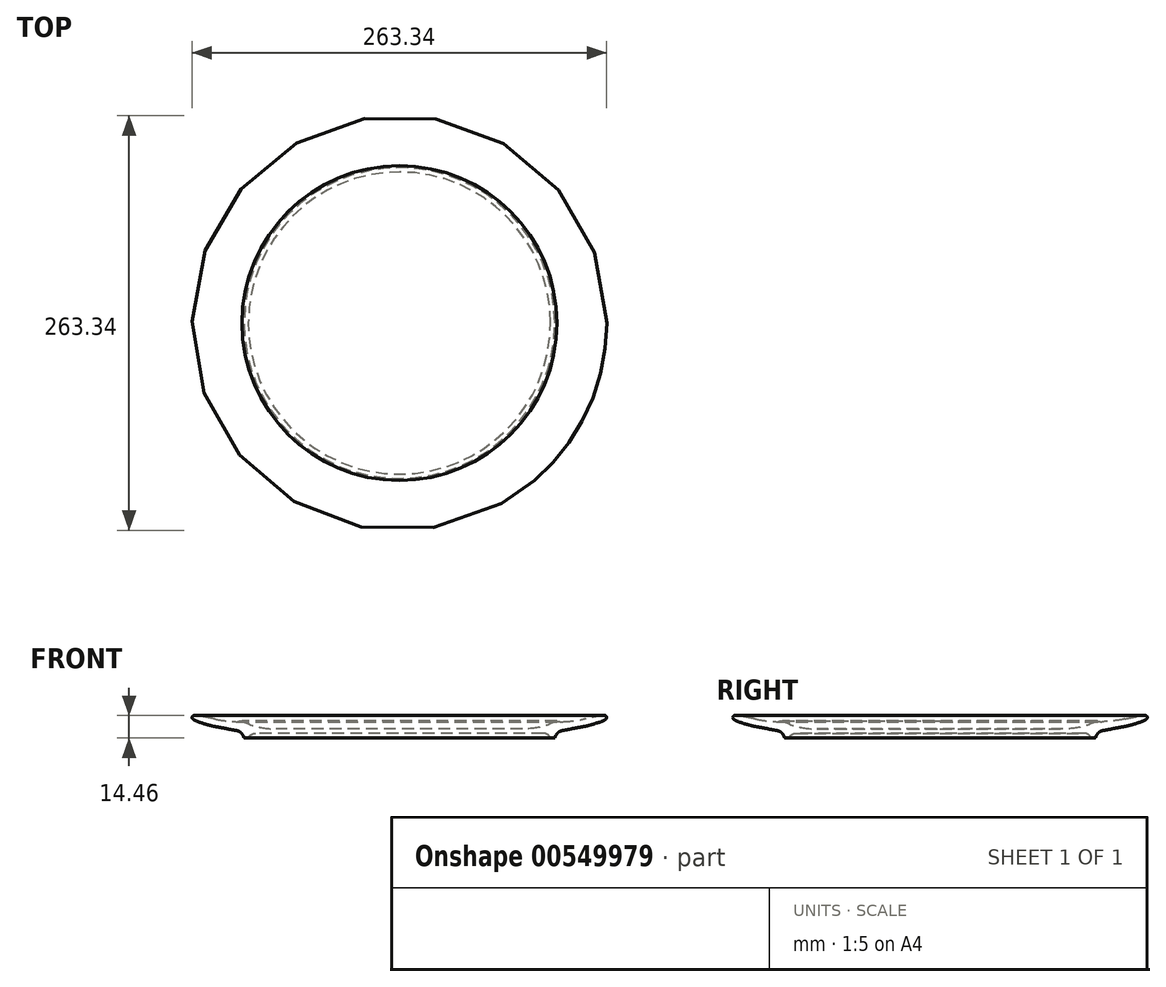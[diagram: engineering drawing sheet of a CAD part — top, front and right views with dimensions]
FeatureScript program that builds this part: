
annotation { "Feature Type Name" : "Feature", "Feature Type Description" : "" }
export const myFeature = defineFeature(function(context is Context, id is Id, definition is map)
    precondition{}
    {
        {
            var Q0;
            Q0=qCreatedBy(makeId("Front.planeOp"),FACE);
            var sketch = newSketch(context, id + "F0", { "sketchPlane" : qUnion([Q0])});
            skLineSegment(sketch, "E0", {"start": v(0, 0) * mm, "end": v(100, 0) * mm});
            skLineSegment(sketch, "E1", {"start": v(100, 0) * mm, "end": v(100, 5) * mm});
            skLineSegment(sketch, "E2", {"start": v(100, 5) * mm, "end": v(129.6, 9.87) * mm, "construction": true});
            skArc(sketch, "E3", {"start": v(100, 5) * mm, "mid": v(101.61, 4.7) * mm, "end": v(103.25, 4.64) * mm});
            skArc(sketch, "E4", {"start": v(103.25, 4.64) * mm, "mid": v(110.44, 5.2) * mm, "end": v(117.56, 6.42) * mm});
            skArc(sketch, "E5", {"start": v(117.56, 6.42) * mm, "mid": v(123.67, 7.65) * mm, "end": v(129.81, 8.65) * mm});
            skArc(sketch, "E6", {"start": v(129.81, 8.65) * mm, "mid": v(130.74, 8.53) * mm, "end": v(131.47, 7.95) * mm});
            skArc(sketch, "E7", {"start": v(131.47, 7.95) * mm, "mid": v(131.67, 7.34) * mm, "end": v(131.47, 6.73) * mm});
            skArc(sketch, "E8", {"start": v(131.47, 6.73) * mm, "mid": v(130.73, 5.96) * mm, "end": v(129.81, 5.42) * mm});
            skArc(sketch, "E9", {"start": v(129.81, 5.42) * mm, "mid": v(123.23, 3.08) * mm, "end": v(116.42, 1.45) * mm});
            skArc(sketch, "E10", {"start": v(116.42, 1.45) * mm, "mid": v(109.68, 0.18) * mm, "end": v(102.94, -1.17) * mm});
            skArc(sketch, "E11", {"start": v(102.94, -1.17) * mm, "mid": v(101.5, -1.72) * mm, "end": v(100.33, -2.7) * mm});
            skArc(sketch, "E12", {"start": v(100.33, -2.7) * mm, "mid": v(99.32, -4.15) * mm, "end": v(98.67, -5.8) * mm});
            skLineSegment(sketch, "E13", {"start": v(98.67, -5.8) * mm, "end": v(95.96, -5.8) * mm});
            skLineSegment(sketch, "E14", {"start": v(95.96, -5.8) * mm, "end": v(95.91, -5.67) * mm});
            skLineSegment(sketch, "E15", {"start": v(91.32, -2.65) * mm, "end": v(0, -2.65) * mm});
            skLineSegment(sketch, "E16", {"start": v(0, 0) * mm, "end": v(0, -2.65) * mm});
            skPoint(sketch, "E17.visualSharp", {"position": v(94.61, -2.65) * mm});
            skArc(sketch, "E17.filletArc", {"start": v(95.91, -5.67) * mm, "mid": v(94.07, -3.47) * mm, "end": v(91.32, -2.65) * mm});
            skSolve(sketch);
        }
        {
            var Q0;
            Q0=makeQuery(id+"F0.imprint","IMPRINT",FACE,{"disambiguationData":[TD([[makeQuery(id+"F0.imprint","IMPRINT",EDGE,{"derivedFrom":sQuery(id+"F0.wireOp",EDGE,"E0")}),-1.0]])]});
            var Q1;
            Q1=sQuery(id+"F0.wireOp",EDGE,"E16");
            revolve(context, id + "F1", {"entities" : qUnion([Q0]), "axis" : qUnion([Q1]), "revolveType" : RevolveType.FULL});
        }
        {
            var Q0;
            Q0=makeQuery(id+"F1.opRevolve","SWEPT_EDGE",EDGE,{"disambiguationData":[OSD([sQuery(id+"F0.wireOp",EDGE,"E0"),sQuery(id+"F0.wireOp",EDGE,"E1")])]});
            fillet(context, id + "F2", {"entities" : qUnion([Q0]), "radius" : 50 * mm, "tangentPropagation" : true, "allowEdgeOverflow" : false});
        }
    });
